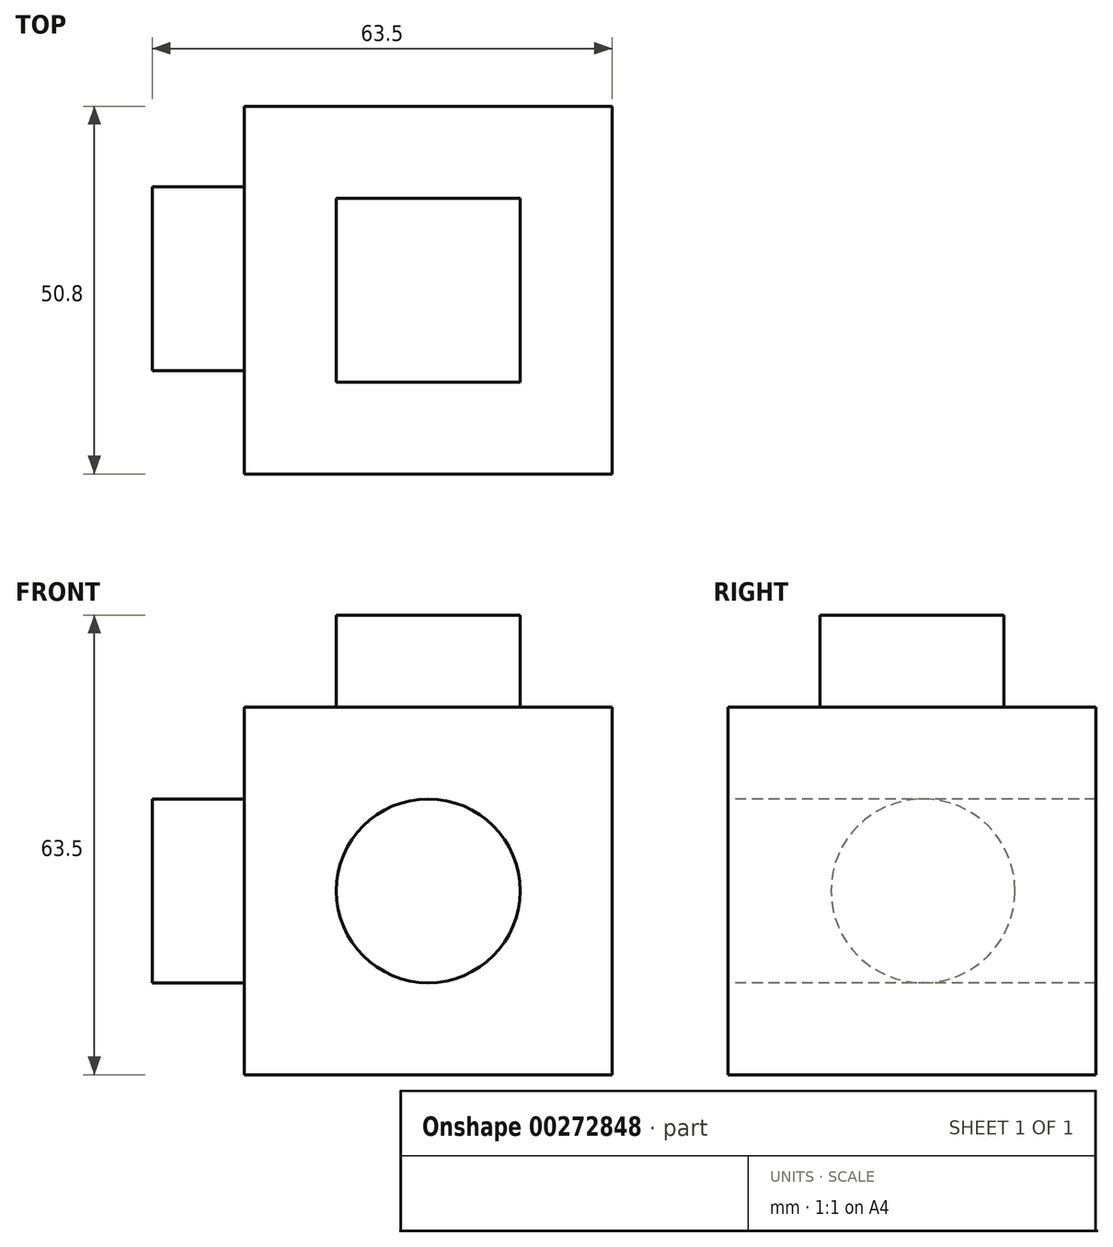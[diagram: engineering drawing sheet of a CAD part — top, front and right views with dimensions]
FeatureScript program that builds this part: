
annotation { "Feature Type Name" : "Feature", "Feature Type Description" : "" }
export const myFeature = defineFeature(function(context is Context, id is Id, definition is map)
    precondition{}
    {
        {
            var Q0;
            Q0=qCreatedBy(makeId("Front.planeOp"),FACE);
            var sketch = newSketch(context, id + "F0", { "sketchPlane" : qUnion([Q0])});
            skLineSegment(sketch, "E0.bottom", {"start": v(0, 0) * mm, "end": v(-50.8, 0) * mm});
            skLineSegment(sketch, "E0.top", {"start": v(0, 50.8) * mm, "end": v(-50.8, 50.8) * mm});
            skLineSegment(sketch, "E0.left", {"start": v(0, 0) * mm, "end": v(0, 50.8) * mm});
            skLineSegment(sketch, "E0.right", {"start": v(-50.8, 0) * mm, "end": v(-50.8, 50.8) * mm});
            skSolve(sketch);
        }
        {
            var Q0;
            Q0 = qSketchRegion(id + "F0", true);
            extrude(context, id + "F1", {"entities" : qUnion([Q0]), "depth" : 50.8 * mm});
        }
        {
            var Q0;
            Q0=makeQuery(id+"F1.opExtrude","CAP_FACE",FACE,{"disambiguationData":[OSD([sQuery(id+"F0.wireOp",EDGE,"E0.bottom"),sQuery(id+"F0.wireOp",EDGE,"E0.top"),sQuery(id+"F0.wireOp",EDGE,"E0.left"),sQuery(id+"F0.wireOp",EDGE,"E0.right")])],"isStart":false});
            var sketch = newSketch(context, id + "F2", { "sketchPlane" : qUnion([Q0])});
            skCircle(sketch, "E1", {"center": v(-25.4, 25.4) * mm, "radius": 12.7 * mm});
            skSolve(sketch);
        }
        {
            var Q0;
            Q0=makeQuery(id+"F2.imprint","IMPRINT",FACE,{"disambiguationData":[TD([[makeQuery(id+"F2.imprint","IMPRINT",EDGE,{"derivedFrom":sQuery(id+"F2.wireOp",EDGE,"E1")}),1.0]])]});
            extrude(context, id + "F3", {"entities" : qUnion([Q0]), "operationType" : NewBodyOperationType.REMOVE, "oppositeDirection" : true, "depth" : 50.8 * mm});
        }
        {
            var Q0;
            Q0=makeQuery(id+"F1.opExtrude","SWEPT_FACE",FACE,{"disambiguationData":[OSD([sQuery(id+"F0.wireOp",EDGE,"E0.right")])]});
            var sketch = newSketch(context, id + "F4", { "sketchPlane" : qUnion([Q0])});
            skCircle(sketch, "E2", {"center": v(23.87, 25.4) * mm, "radius": 12.7 * mm});
            skSolve(sketch);
        }
        {
            var Q0;
            Q0=makeQuery(id+"F4.imprint","IMPRINT",FACE,{"disambiguationData":[TD([[makeQuery(id+"F4.imprint","IMPRINT",EDGE,{"derivedFrom":sQuery(id+"F4.wireOp",EDGE,"E2")}),1.0]])]});
            extrude(context, id + "F5", {"entities" : qUnion([Q0]), "operationType" : NewBodyOperationType.ADD, "depth" : 12.7 * mm});
        }
        {
            var Q0;
            Q0=makeQuery(id+"F1.opExtrude","SWEPT_FACE",FACE,{"disambiguationData":[OSD([sQuery(id+"F0.wireOp",EDGE,"E0.top")])]});
            var sketch = newSketch(context, id + "F6", { "sketchPlane" : qUnion([Q0])});
            skLineSegment(sketch, "E3.bottom", {"start": v(-38.1, -12.7) * mm, "end": v(-12.7, -12.7) * mm});
            skLineSegment(sketch, "E3.top", {"start": v(-38.1, -38.1) * mm, "end": v(-12.7, -38.1) * mm});
            skLineSegment(sketch, "E3.left", {"start": v(-38.1, -12.7) * mm, "end": v(-38.1, -38.1) * mm});
            skLineSegment(sketch, "E3.right", {"start": v(-12.7, -12.7) * mm, "end": v(-12.7, -38.1) * mm});
            skSolve(sketch);
        }
        {
            var Q0;
            Q0=makeQuery(id+"F6.imprint","IMPRINT",FACE,{"disambiguationData":[TD([[makeQuery(id+"F6.imprint","IMPRINT",EDGE,{"derivedFrom":sQuery(id+"F6.wireOp",EDGE,"E3.bottom")}),-1.0]])]});
            extrude(context, id + "F7", {"entities" : qUnion([Q0]), "operationType" : NewBodyOperationType.ADD, "depth" : 12.7 * mm});
        }
    });
